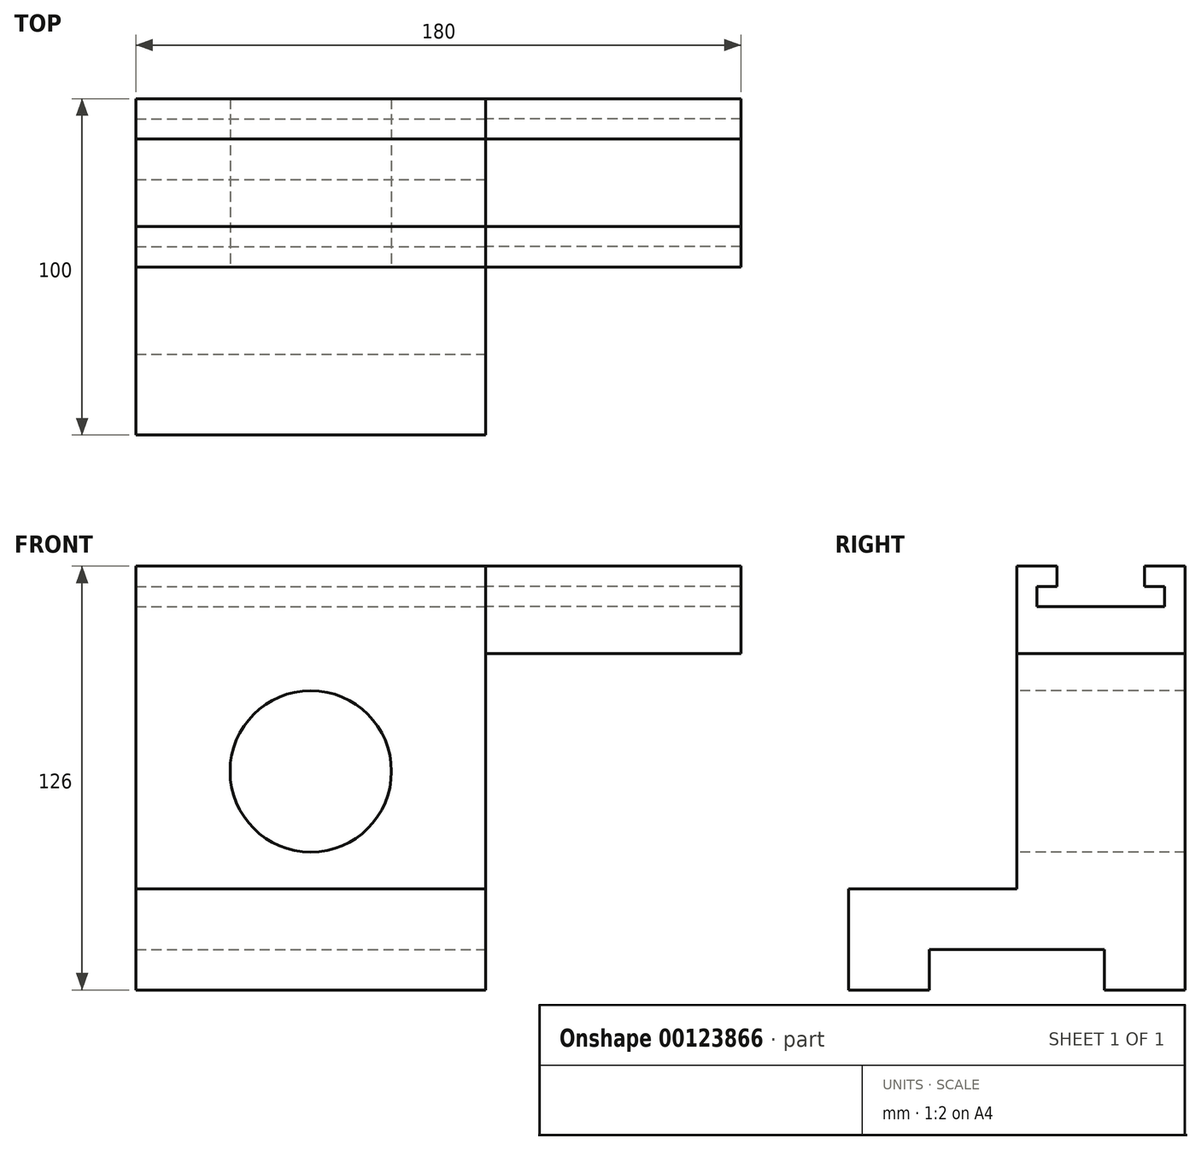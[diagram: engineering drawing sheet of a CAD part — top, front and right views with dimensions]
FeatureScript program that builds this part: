
annotation { "Feature Type Name" : "Feature", "Feature Type Description" : "" }
export const myFeature = defineFeature(function(context is Context, id is Id, definition is map)
    precondition{}
    {
        {
            var Q0;
            Q0=qCreatedBy(makeId("Right.planeOp"),FACE);
            var sketch = newSketch(context, id + "F0", { "sketchPlane" : qUnion([Q0])});
            skLineSegment(sketch, "E0", {"start": v(26, 0) * mm, "end": v(50, 0) * mm});
            skLineSegment(sketch, "E1", {"start": v(-26, 0) * mm, "end": v(-50, 0) * mm});
            skLineSegment(sketch, "E2", {"start": v(26, 0) * mm, "end": v(26, 12) * mm});
            skLineSegment(sketch, "E3", {"start": v(-26, 0) * mm, "end": v(-26, 12) * mm});
            skLineSegment(sketch, "E4", {"start": v(-26, 12) * mm, "end": v(26, 12) * mm});
            skLineSegment(sketch, "E5", {"start": v(-50, 0) * mm, "end": v(-50, 30) * mm});
            skLineSegment(sketch, "E6", {"start": v(-50, 30) * mm, "end": v(0, 30) * mm});
            skLineSegment(sketch, "E7", {"start": v(0, 30) * mm, "end": v(0, 100) * mm});
            skLineSegment(sketch, "E8", {"start": v(0, 100) * mm, "end": v(50, 100) * mm});
            skLineSegment(sketch, "E9", {"start": v(50, 100) * mm, "end": v(50, 0) * mm});
            skLineSegment(sketch, "E10", {"start": v(50, 100) * mm, "end": v(50, 126) * mm});
            skLineSegment(sketch, "E11", {"start": v(50, 126) * mm, "end": v(38, 126) * mm});
            skLineSegment(sketch, "E12", {"start": v(38, 126) * mm, "end": v(38, 120) * mm});
            skLineSegment(sketch, "E13", {"start": v(38, 120) * mm, "end": v(44, 120) * mm});
            skLineSegment(sketch, "E14", {"start": v(44, 120) * mm, "end": v(44, 114) * mm});
            skLineSegment(sketch, "E15", {"start": v(0, 100) * mm, "end": v(0, 126) * mm});
            skLineSegment(sketch, "E16", {"start": v(0, 126) * mm, "end": v(12, 126) * mm});
            skLineSegment(sketch, "E17", {"start": v(12, 126) * mm, "end": v(12, 120) * mm});
            skLineSegment(sketch, "E18", {"start": v(12, 120) * mm, "end": v(6, 120) * mm});
            skLineSegment(sketch, "E19", {"start": v(6, 120) * mm, "end": v(6, 114) * mm});
            skLineSegment(sketch, "E20", {"start": v(6, 114) * mm, "end": v(44, 114) * mm});
            skSolve(sketch);
        }
        {
            var Q0;
            Q0=makeQuery(id+"F0.imprint","IMPRINT",FACE,{"disambiguationData":[TD([[makeQuery(id+"F0.imprint","IMPRINT",EDGE,{"derivedFrom":sQuery(id+"F0.wireOp",EDGE,"E0")}),1.0]])]});
            var Q1;
            Q1=makeQuery(id+"F0.imprint","IMPRINT",FACE,{"disambiguationData":[TD([[makeQuery(id+"F0.imprint","IMPRINT",EDGE,{"derivedFrom":sQuery(id+"F0.wireOp",EDGE,"E8")}),1.0]])]});
            extrude(context, id + "F1", {"entities" : qUnion([Q0, Q1]), "oppositeDirection" : true, "depth" : 104 * mm});
        }
        {
            var Q0;
            Q0=makeQuery(id+"F0.imprint","IMPRINT",FACE,{"disambiguationData":[TD([[makeQuery(id+"F0.imprint","IMPRINT",EDGE,{"derivedFrom":sQuery(id+"F0.wireOp",EDGE,"E8")}),1.0]])]});
            var Q1;
            Q1=sQuery(id+"F0.wireOp",EDGE,"E15");
            var Q2;
            Q2=sQuery(id+"F0.wireOp",EDGE,"E8");
            var Q3;
            Q3=sQuery(id+"F0.wireOp",EDGE,"E10");
            var Q4;
            Q4=sQuery(id+"F0.wireOp",EDGE,"E20");
            var Q5;
            Q5=sQuery(id+"F0.wireOp",EDGE,"E16");
            var Q6;
            Q6=sQuery(id+"F0.wireOp",EDGE,"E11");
            var Q7;
            Q7=sQuery(id+"F0.wireOp",EDGE,"E19");
            var Q8;
            Q8=sQuery(id+"F0.wireOp",EDGE,"E17");
            var Q9;
            Q9=sQuery(id+"F0.wireOp",EDGE,"E14");
            var Q10;
            Q10=sQuery(id+"F0.wireOp",EDGE,"E12");
            var Q11;
            Q11=sQuery(id+"F0.wireOp",EDGE,"E18");
            var Q12;
            Q12=sQuery(id+"F0.wireOp",EDGE,"E13");
            extrude(context, id + "F2", {"entities" : qUnion([Q0]), "surfaceEntities" : qUnion([Q1, Q2, Q3, Q4, Q5, Q6, Q7, Q8, Q9, Q10, Q11, Q12]), "depth" : 76 * mm});
        }
        {
            var Q0;
            Q0=makeQuery(id+"F1.opExtrude","SWEPT_FACE",FACE,{"disambiguationData":[OSD([sQuery(id+"F0.wireOp",EDGE,"E7"),sQuery(id+"F0.wireOp",EDGE,"E15")])]});
            var sketch = newSketch(context, id + "F3", { "sketchPlane" : qUnion([Q0])});
            skCircle(sketch, "E21", {"center": v(-52, 65) * mm, "radius": 24 * mm});
            skSolve(sketch);
        }
        {
            var Q0;
            Q0=makeQuery(id+"F3.imprint","IMPRINT",FACE,{"disambiguationData":[TD([[makeQuery(id+"F3.imprint","IMPRINT",EDGE,{"derivedFrom":sQuery(id+"F3.wireOp",EDGE,"E21")}),1.0]])]});
            extrude(context, id + "F4", {"entities" : qUnion([Q0]), "operationType" : NewBodyOperationType.REMOVE, "oppositeDirection" : true, "depth" : 50 * mm});
        }
    });
